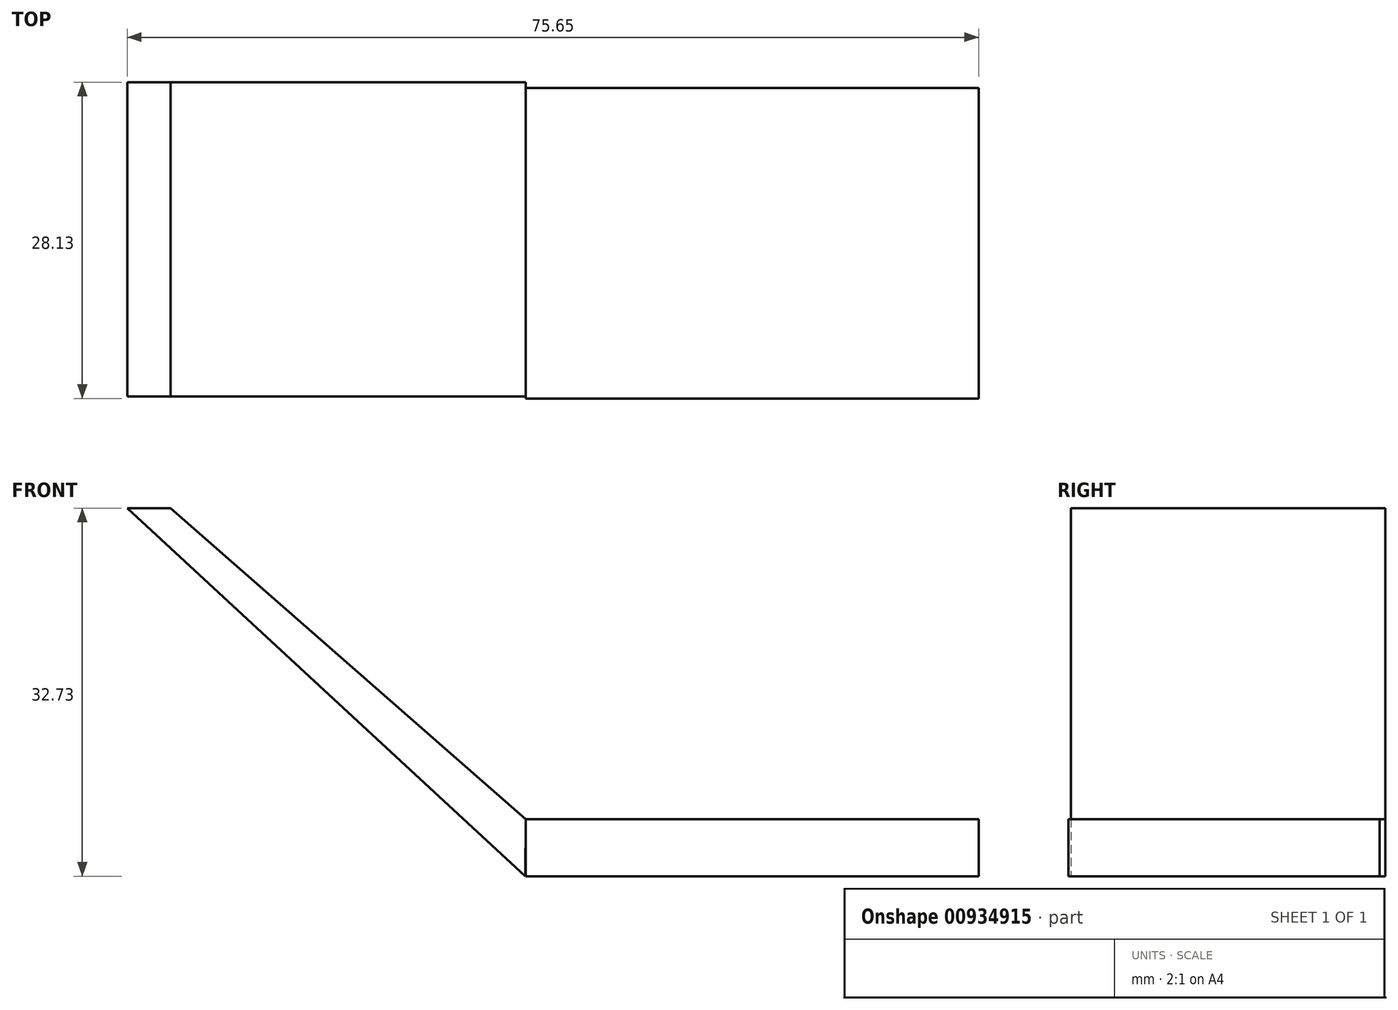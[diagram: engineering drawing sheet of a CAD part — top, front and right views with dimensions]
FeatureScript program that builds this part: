
annotation { "Feature Type Name" : "Feature", "Feature Type Description" : "" }
export const myFeature = defineFeature(function(context is Context, id is Id, definition is map)
    precondition{}
    {
        {
            var Q0;
            Q0=qCreatedBy(makeId("Top.planeOp"),FACE);
            var sketch = newSketch(context, id + "F0", { "sketchPlane" : qUnion([Q0])});
            skLineSegment(sketch, "E0.bottom", {"start": v(0, -19.75) * mm, "end": v(-40.26, -19.75) * mm});
            skLineSegment(sketch, "E0.top", {"start": v(0, 13.46) * mm, "end": v(-40.26, 13.46) * mm});
            skLineSegment(sketch, "E0.left", {"start": v(0, -19.75) * mm, "end": v(0, 13.46) * mm});
            skLineSegment(sketch, "E0.right", {"start": v(-40.26, -19.75) * mm, "end": v(-40.26, 13.46) * mm});
            skSolve(sketch);
        }
        {
            var Q0;
            Q0=makeQuery(id+"F0.imprint","IMPRINT",FACE,{"disambiguationData":[TD([[makeQuery(id+"F0.imprint","IMPRINT",EDGE,{"derivedFrom":sQuery(id+"F0.wireOp",EDGE,"E0.bottom")}),-1.0]])]});
            extrude(context, id + "F1", {"entities" : qUnion([Q0]), "depth" : 5.08 * mm, "offsetDistance" : 25.4 * mm});
        }
        {
            var Q0;
            Q0=qCreatedBy(makeId("Front.planeOp"),FACE);
            var sketch = newSketch(context, id + "F2", { "sketchPlane" : qUnion([Q0])});
            skLineSegment(sketch, "E1", {"start": v(-40.27, 0) * mm, "end": v(-75.65, 32.73) * mm});
            skLineSegment(sketch, "E2", {"start": v(-75.65, 32.73) * mm, "end": v(-71.81, 32.73) * mm});
            skLineSegment(sketch, "E3", {"start": v(-71.81, 32.73) * mm, "end": v(-40.26, 5.08) * mm});
            skLineSegment(sketch, "E4", {"start": v(-40.26, 5.08) * mm, "end": v(-40.27, 0) * mm});
            skSolve(sketch);
        }
        {
            var Q0;
            Q0=makeQuery(id+"F2.imprint","IMPRINT",FACE,{"disambiguationData":[TD([[makeQuery(id+"F2.imprint","IMPRINT",EDGE,{"derivedFrom":sQuery(id+"F2.wireOp",EDGE,"E1")}),-1.0]])]});
            extrude(context, id + "F3", {"entities" : qUnion([Q0]), "endBound" : BoundingType.SYMMETRIC, "oppositeDirection" : true, "depth" : 27.94 * mm, "offsetDistance" : 25.4 * mm});
        }
        {
            var Q0;
            Q0=makeQuery(id+"F1.opExtrude","SWEPT_FACE",FACE,{"disambiguationData":[OSD([sQuery(id+"F0.wireOp",EDGE,"E0.bottom")])]});
            extrude(context, id + "F4", {"entities" : qUnion([Q0]), "operationType" : NewBodyOperationType.REMOVE, "oppositeDirection" : true, "depth" : 5.6 * mm, "offsetDistance" : 25.4 * mm});
        }
    });
